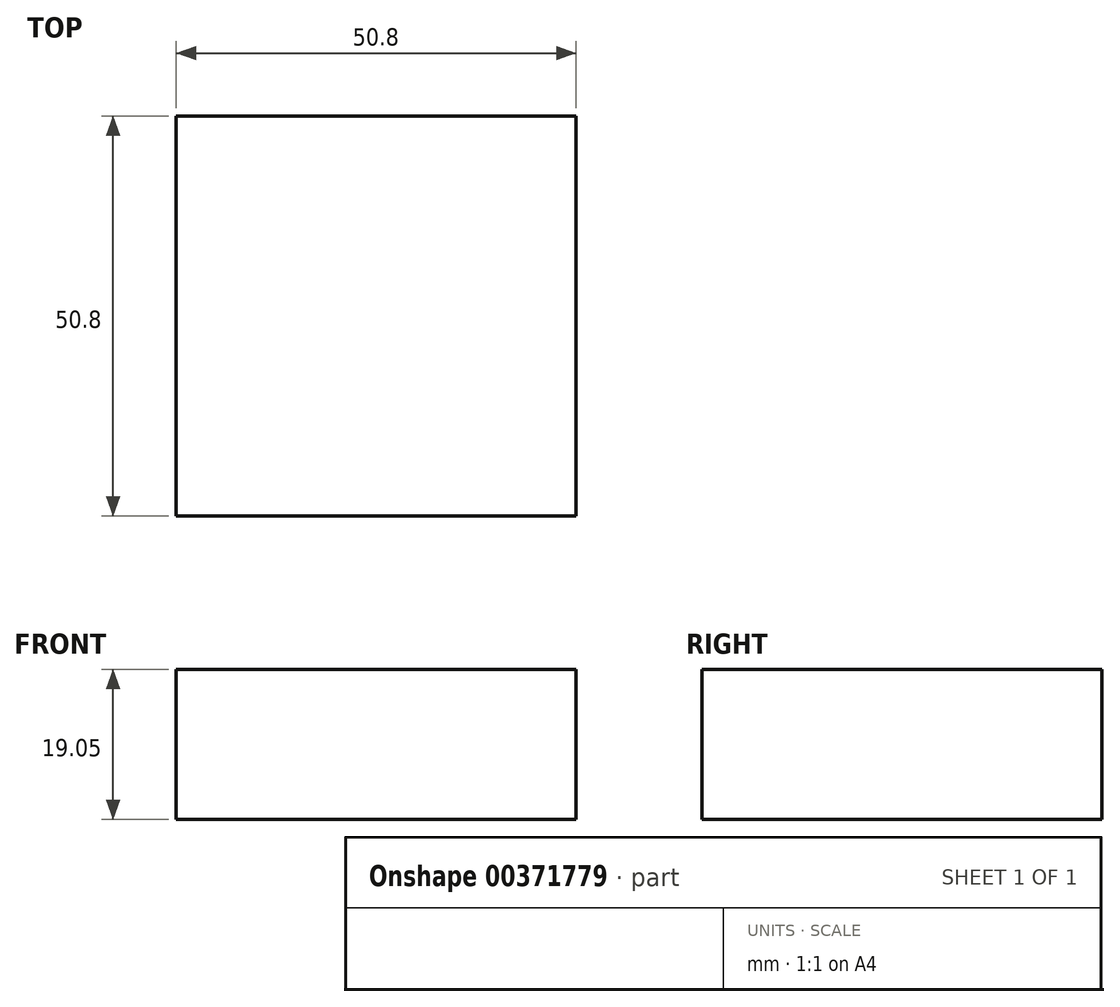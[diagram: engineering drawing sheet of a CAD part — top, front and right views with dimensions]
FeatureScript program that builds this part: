
annotation { "Feature Type Name" : "Feature", "Feature Type Description" : "" }
export const myFeature = defineFeature(function(context is Context, id is Id, definition is map)
    precondition{}
    {
        {
            var Q0;
            Q0=qCreatedBy(makeId("Top.planeOp"),FACE);
            var sketch = newSketch(context, id + "F0", { "sketchPlane" : qUnion([Q0])});
            skLineSegment(sketch, "E0.bottom", {"start": v(25.4, -25.4) * mm, "end": v(-25.4, -25.4) * mm});
            skLineSegment(sketch, "E0.top", {"start": v(25.4, 25.4) * mm, "end": v(-25.4, 25.4) * mm});
            skLineSegment(sketch, "E0.left", {"start": v(25.4, -25.4) * mm, "end": v(25.4, 25.4) * mm});
            skLineSegment(sketch, "E0.right", {"start": v(-25.4, -25.4) * mm, "end": v(-25.4, 25.4) * mm});
            skPoint(sketch, "E0.middle", {"position": v(0, 0) * mm});
            skSolve(sketch);
        }
        {
            var Q0;
            Q0 = qSketchRegion(id + "F0", true);
            extrude(context, id + "F1", {"entities" : qUnion([Q0]), "depth" : 19.05 * mm});
        }
    });
